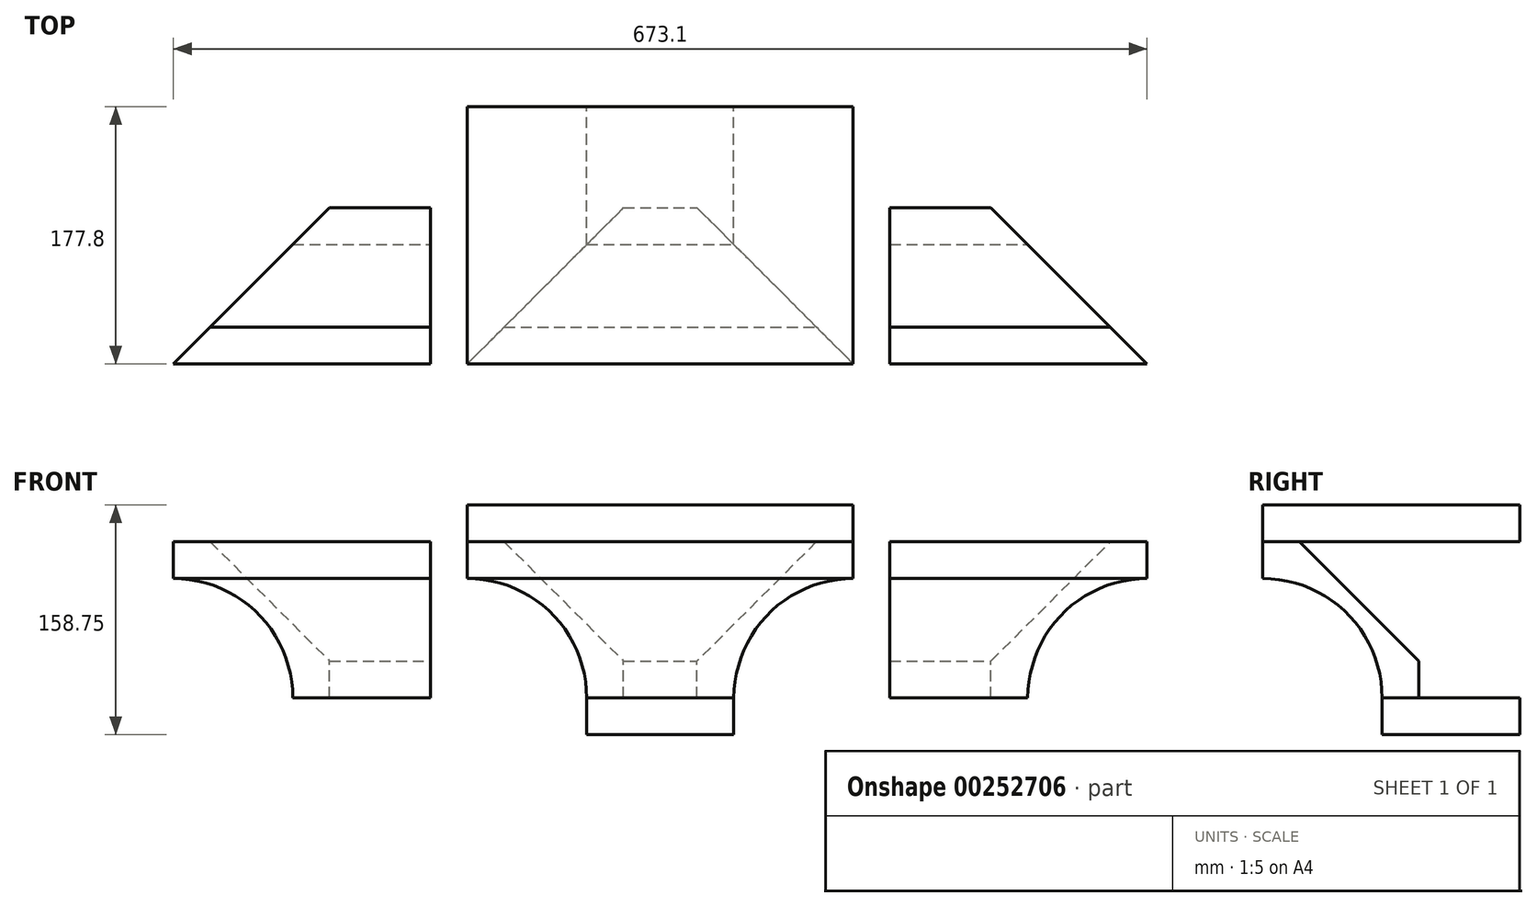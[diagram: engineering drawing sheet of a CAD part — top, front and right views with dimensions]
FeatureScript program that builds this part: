
annotation { "Feature Type Name" : "Feature", "Feature Type Description" : "" }
export const myFeature = defineFeature(function(context is Context, id is Id, definition is map)
    precondition{}
    {
        {
            var Q0;
            Q0=qCreatedBy(makeId("Right.planeOp"),FACE);
            var sketch = newSketch(context, id + "F0", { "sketchPlane" : qUnion([Q0])});
            skLineSegment(sketch, "E0", {"start": v(0, 0) * mm, "end": v(0, 25.4) * mm});
            skLineSegment(sketch, "E1", {"start": v(0, 25.4) * mm, "end": v(-82.55, 107.95) * mm});
            skLineSegment(sketch, "E2", {"start": v(-82.55, 107.95) * mm, "end": v(-107.95, 107.95) * mm});
            skLineSegment(sketch, "E3", {"start": v(-107.95, 107.95) * mm, "end": v(-107.95, 82.55) * mm});
            skLineSegment(sketch, "E4", {"start": v(-107.95, 82.55) * mm, "end": v(-107.95, 82.55) * mm});
            skLineSegment(sketch, "E5", {"start": v(-25.4, 0) * mm, "end": v(0, 0) * mm});
            skArc(sketch, "E6", {"start": v(-107.95, 82.55) * mm, "mid": v(-49.58, 58.37) * mm, "end": v(-25.4, 0) * mm});
            skSolve(sketch);
        }
        {
            var Q0;
            Q0=qSketchRegion(id+"F0",true);
            extrude(context, id + "F1", {"entities" : qUnion([Q0]), "endBound" : BoundingType.SYMMETRIC, "oppositeDirection" : true, "depth" : 673.1 * mm});
        }
        {
            var Q0;
            Q0=makeQuery(id+"F1.opExtrude","SWEPT_FACE",FACE,{"disambiguationData":[OSD([sQuery(id+"F0.wireOp",EDGE,"E2")])]});
            var sketch = newSketch(context, id + "F2", { "sketchPlane" : qUnion([Q0])});
            skLineSegment(sketch, "E7", {"start": v(-336.55, -107.95) * mm, "end": v(-228.6, 0) * mm});
            skLineSegment(sketch, "E8", {"start": v(-228.6, 0) * mm, "end": v(-336.55, 0) * mm});
            skLineSegment(sketch, "E9", {"start": v(-336.55, 0) * mm, "end": v(-336.55, -107.95) * mm});
            skLineSegment(sketch, "E10", {"start": v(336.55, -107.95) * mm, "end": v(336.55, 0) * mm});
            skLineSegment(sketch, "E11", {"start": v(336.55, 0) * mm, "end": v(228.6, 0) * mm});
            skLineSegment(sketch, "E12", {"start": v(228.6, 0) * mm, "end": v(336.55, -107.95) * mm});
            skLineSegment(sketch, "E13", {"start": v(-158.75, 0) * mm, "end": v(-158.75, -107.95) * mm});
            skLineSegment(sketch, "E14", {"start": v(-158.75, -107.95) * mm, "end": v(-133.35, -107.95) * mm});
            skLineSegment(sketch, "E15", {"start": v(-133.35, -107.95) * mm, "end": v(-25.4, 0) * mm});
            skLineSegment(sketch, "E16", {"start": v(-25.4, 0) * mm, "end": v(-158.75, 0) * mm});
            skLineSegment(sketch, "E17", {"start": v(158.75, 0) * mm, "end": v(158.75, -107.95) * mm});
            skLineSegment(sketch, "E18", {"start": v(158.75, -107.95) * mm, "end": v(133.35, -107.95) * mm});
            skLineSegment(sketch, "E19", {"start": v(133.35, -107.95) * mm, "end": v(25.4, 0) * mm});
            skLineSegment(sketch, "E20", {"start": v(25.4, 0) * mm, "end": v(158.75, 0) * mm});
            skSolve(sketch);
        }
        {
            var Q0;
            Q0=qSketchRegion(id+"F2",true);
            extrude(context, id + "F3", {"entities" : qUnion([Q0]), "operationType" : NewBodyOperationType.REMOVE, "endBound" : BoundingType.THROUGH_ALL, "oppositeDirection" : true, "depth" : 25.4 * mm});
        }
        {
            var Q0;
            Q0=makeQuery(id+"F3.boolean.opBoolean","SPLIT",FACE,{"disambiguationData":[TD([makeQuery(id+"F3.opExtrude","SWEPT_FACE",FACE,{"disambiguationData":[OSD([sQuery(id+"F2.wireOp",EDGE,"E15")])]})])],"derivedFrom":makeQuery(id+"F1.opExtrude","SWEPT_FACE",FACE,{"disambiguationData":[OSD([sQuery(id+"F0.wireOp",EDGE,"E5")])]})});
            var sketch = newSketch(context, id + "F4", { "sketchPlane" : qUnion([Q0])});
            skLineSegment(sketch, "E21.bottom", {"start": v(-50.8, 25.4) * mm, "end": v(50.8, 25.4) * mm});
            skLineSegment(sketch, "E21.top", {"start": v(-50.8, -69.85) * mm, "end": v(50.8, -69.85) * mm});
            skLineSegment(sketch, "E21.left", {"start": v(-50.8, 25.4) * mm, "end": v(-50.8, -69.85) * mm});
            skLineSegment(sketch, "E21.right", {"start": v(50.8, 25.4) * mm, "end": v(50.8, -69.85) * mm});
            skSolve(sketch);
        }
        {
            var Q0;
            Q0=qSketchRegion(id+"F4",true);
            extrude(context, id + "F5", {"entities" : qUnion([Q0]), "depth" : 25.4 * mm});
        }
        {
            var Q0;
            Q0=makeQuery(id+"F3.boolean.opBoolean","SPLIT",FACE,{"disambiguationData":[TD([makeQuery(id+"F3.opExtrude","SWEPT_FACE",FACE,{"disambiguationData":[OSD([sQuery(id+"F2.wireOp",EDGE,"E15")])]})])],"derivedFrom":makeQuery(id+"F1.opExtrude","SWEPT_FACE",FACE,{"disambiguationData":[OSD([sQuery(id+"F0.wireOp",EDGE,"E2")])]})});
            var sketch = newSketch(context, id + "F6", { "sketchPlane" : qUnion([Q0])});
            skLineSegment(sketch, "E22.bottom", {"start": v(-133.35, -107.95) * mm, "end": v(133.35, -107.95) * mm});
            skLineSegment(sketch, "E22.top", {"start": v(-133.35, 69.85) * mm, "end": v(133.35, 69.85) * mm});
            skLineSegment(sketch, "E22.left", {"start": v(-133.35, 69.85) * mm, "end": v(-133.35, -107.95) * mm});
            skLineSegment(sketch, "E22.right", {"start": v(133.35, 69.85) * mm, "end": v(133.35, -107.95) * mm});
            skSolve(sketch);
        }
        {
            var Q0;
            Q0=qSketchRegion(id+"F6",true);
            extrude(context, id + "F7", {"entities" : qUnion([Q0]), "depth" : 25.4 * mm});
        }
    });
